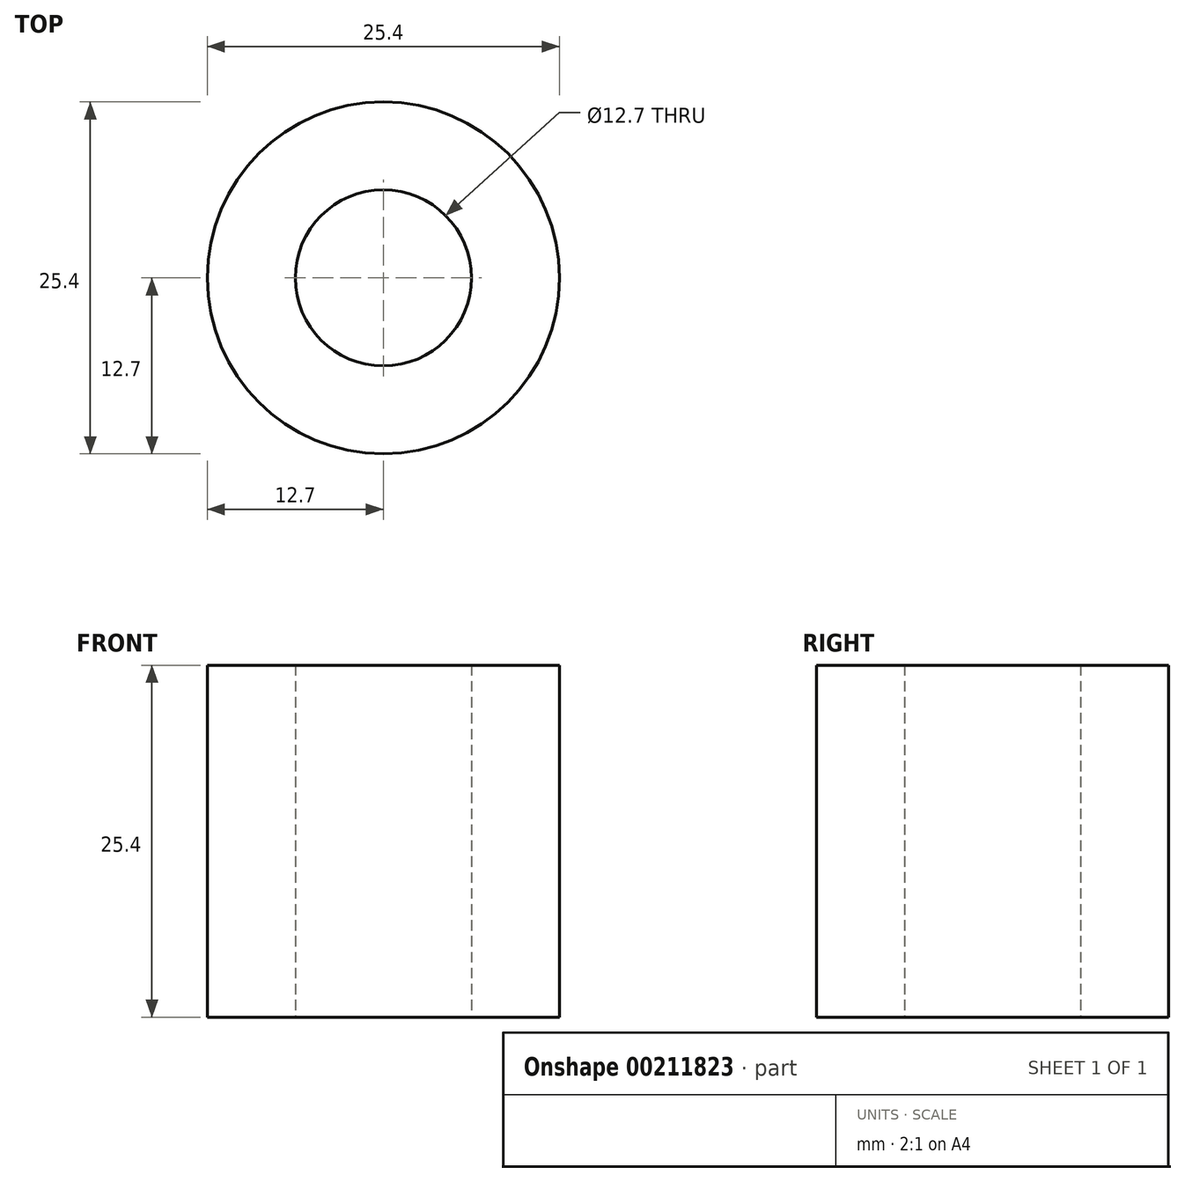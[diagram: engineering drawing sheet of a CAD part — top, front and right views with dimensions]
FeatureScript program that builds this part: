
annotation { "Feature Type Name" : "Feature", "Feature Type Description" : "" }
export const myFeature = defineFeature(function(context is Context, id is Id, definition is map)
    precondition{}
    {
        {
            var Q0;
            Q0=qCreatedBy(makeId("Top.planeOp"),FACE);
            var sketch = newSketch(context, id + "F0", { "sketchPlane" : qUnion([Q0])});
            skCircle(sketch, "E0", {"center": v(0, 0) * mm, "radius": 12.7 * mm});
            skCircle(sketch, "E1", {"center": v(0, 0) * mm, "radius": 6.35 * mm});
            skSolve(sketch);
        }
        {
            var Q0;
            Q0=makeQuery(id+"F0.imprint","IMPRINT",FACE,{"disambiguationData":[TD([[makeQuery(id+"F0.imprint","IMPRINT",EDGE,{"derivedFrom":sQuery(id+"F0.wireOp",EDGE,"E0")}),1.0]])]});
            extrude(context, id + "F1", {"entities" : qUnion([Q0]), "depth" : 25.4 * mm});
        }
    });
